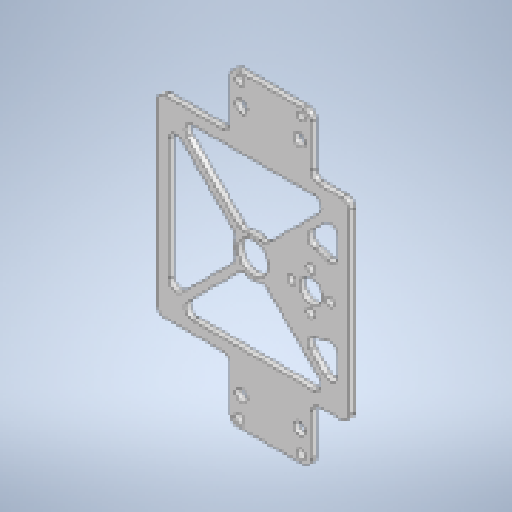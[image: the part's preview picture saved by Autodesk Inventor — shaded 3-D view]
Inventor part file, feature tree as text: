
AUTODESK INVENTOR PART (.ipt)
format: ipt  version: 2025.1 (Build 291241000, 241)  size: 360,448 bytes
history: native  units: mm
features: reference x20, extrude x7, sketch x7, other x6, fillet x3, projected_geometry x2
ambient origin geometry x8: Origin, YZ Plane, XZ Plane, XY Plane, X Axis, Y Axis, Z Axis, Center Point
bodies: Body1 (feature_tree)
feature tree (45):
  other  "ソリッド1"
  extrude  "押し出し1"  Depth=1.5mm TaperAngle=0.0deg
  extrude  "押し出し2"  Depth=10.0mm TaperAngle=0.0deg
  fillet  "フィレット2"  Radius=2.0mm
  extrude  "押し出し3"  Depth=20.0mm
  extrude  "押し出し4"  Depth=10.0mm
  extrude  "押し出し5"  Depth=2.2mm
  extrude  "押し出し6"  Depth=40.0mm TaperAngle=360.0deg
  fillet  "フィレット3"  [1 undecoded]
  extrude  "押し出し7"  TaperAngle=0.0deg  [1 undecoded]
  fillet  "フィレット4"  [1 undecoded]
  sketch  "スケッチ1"
  reference  "参照1"
  sketch  "スケッチ3"
  projected_geometry  "投影ループ2"
  reference  "参照2"
  reference  "参照3"
  reference  "参照4"
  reference  "参照5"
  reference  "参照6"
  reference  "参照7"
  reference  "参照8"
  reference  "参照9"
  reference  "参照10"
  reference  "参照11"
  reference  "参照12"
  reference  "参照13"
  reference  "参照14"
  reference  "参照15"
  sketch  "スケッチ4"
  other  "スケッチ円形状パターン1"
  sketch  "スケッチ5"
  reference  "参照16"
  reference  "参照17"
  reference  "参照18"
  reference  "参照19"
  sketch  "スケッチ6"
  reference  "参照20"
  sketch  "スケッチ7"
  projected_geometry  "投影ループ3"
  sketch  "スケッチ8"
  other  "<userpath>\Documents\Inventor\Vixen\doutai.iam"
  other  "doutai.iam"
  other  "katasita:1"
  other  "fox:1"
note: 3 required parameter values undecoded (feature->parameter linkage not recoverable at this tier; creation-order binding heuristic only, values carry confidence <= 0.55)
